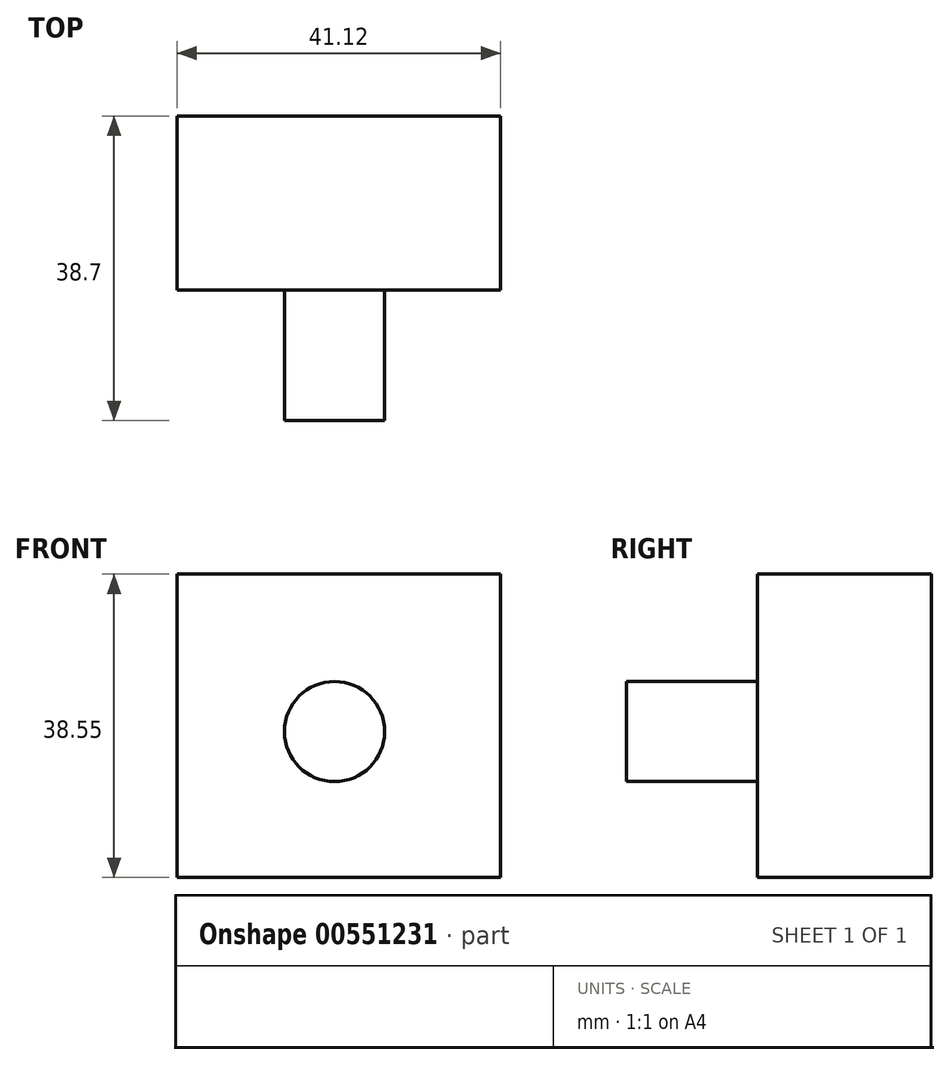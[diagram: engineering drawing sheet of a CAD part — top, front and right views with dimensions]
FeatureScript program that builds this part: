
annotation { "Feature Type Name" : "Feature", "Feature Type Description" : "" }
export const myFeature = defineFeature(function(context is Context, id is Id, definition is map)
    precondition{}
    {
        {
            var Q0;
            Q0=qCreatedBy(makeId("Front.planeOp"),FACE);
            var sketch = newSketch(context, id + "F0", { "sketchPlane" : qUnion([Q0])});
            skLineSegment(sketch, "E0.bottom", {"start": v(-70.3, 47) * mm, "end": v(-29.19, 47) * mm});
            skLineSegment(sketch, "E0.top", {"start": v(-70.3, 8.44) * mm, "end": v(-29.19, 8.44) * mm});
            skLineSegment(sketch, "E0.left", {"start": v(-70.3, 47) * mm, "end": v(-70.3, 8.44) * mm});
            skLineSegment(sketch, "E0.right", {"start": v(-29.19, 47) * mm, "end": v(-29.19, 8.44) * mm});
            skSolve(sketch);
        }
        {
            var Q0;
            Q0=makeQuery(id+"F0.imprint","IMPRINT",FACE,{"disambiguationData":[TD([[makeQuery(id+"F0.imprint","IMPRINT",EDGE,{"derivedFrom":sQuery(id+"F0.wireOp",EDGE,"E0.bottom")}),-1.0]])]});
            extrude(context, id + "F1", {"entities" : qUnion([Q0]), "depth" : 22.1 * mm, "offsetDistance" : 25 * mm});
        }
        {
            var Q0;
            Q0=makeQuery(id+"F1.opExtrude","CAP_FACE",FACE,{"disambiguationData":[OSD([sQuery(id+"F0.wireOp",EDGE,"E0.bottom"),sQuery(id+"F0.wireOp",EDGE,"E0.top"),sQuery(id+"F0.wireOp",EDGE,"E0.left"),sQuery(id+"F0.wireOp",EDGE,"E0.right")])],"isStart":false});
            var sketch = newSketch(context, id + "F2", { "sketchPlane" : qUnion([Q0])});
            skCircle(sketch, "E1", {"center": v(-50.3, 26.98) * mm, "radius": 6.36 * mm});
            skSolve(sketch);
        }
        {
            var Q0;
            Q0=makeQuery(id+"F2.imprint","IMPRINT",FACE,{"disambiguationData":[TD([[makeQuery(id+"F2.imprint","IMPRINT",EDGE,{"derivedFrom":sQuery(id+"F2.wireOp",EDGE,"E1")}),1.0]])]});
            extrude(context, id + "F3", {"entities" : qUnion([Q0]), "operationType" : NewBodyOperationType.ADD, "depth" : 16.6 * mm, "offsetDistance" : 25 * mm});
        }
    });
